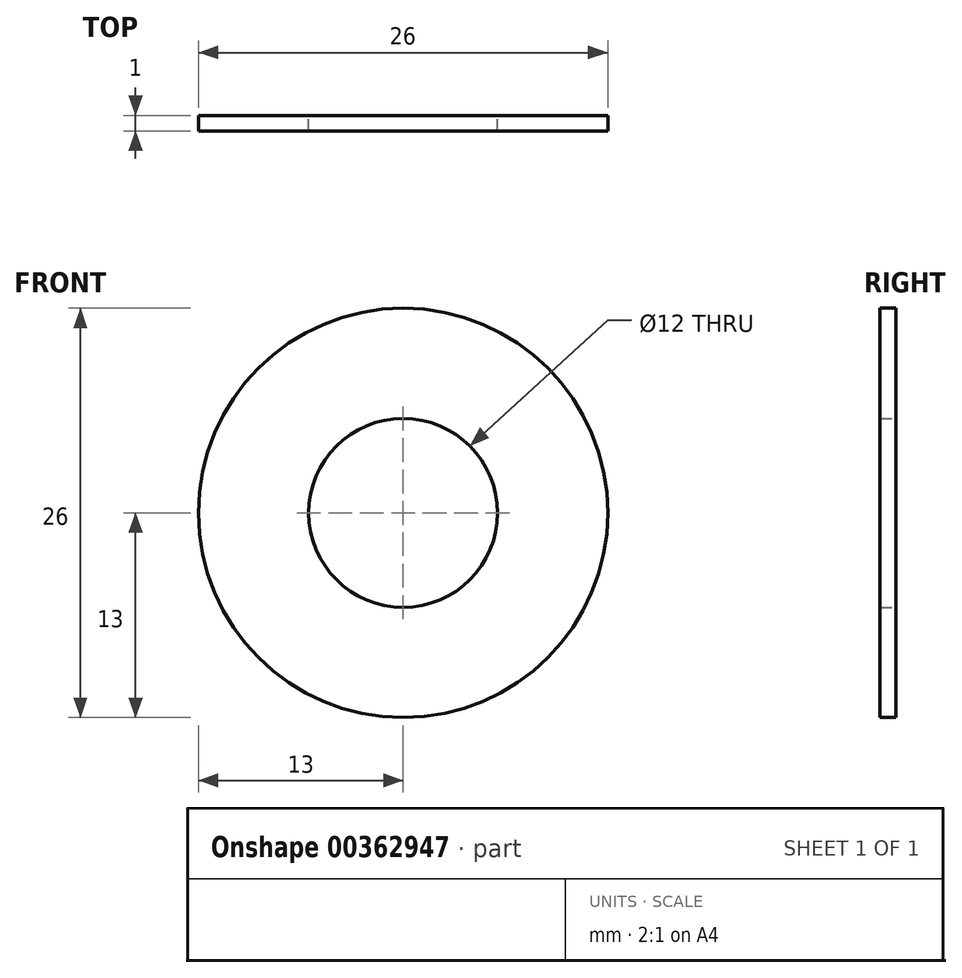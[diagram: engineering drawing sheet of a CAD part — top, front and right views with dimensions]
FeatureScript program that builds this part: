
annotation { "Feature Type Name" : "Feature", "Feature Type Description" : "" }
export const myFeature = defineFeature(function(context is Context, id is Id, definition is map)
    precondition{}
    {
        {
            var Q0;
            Q0=qCreatedBy(makeId("Front.planeOp"),FACE);
            var sketch = newSketch(context, id + "F0", { "sketchPlane" : qUnion([Q0])});
            skCircle(sketch, "E0", {"center": v(0, 0) * mm, "radius": 6 * mm});
            skCircle(sketch, "E1", {"center": v(0, 0) * mm, "radius": 13 * mm});
            skSolve(sketch);
        }
        {
            var Q0;
            Q0=makeQuery(id+"F0.imprint","IMPRINT",FACE,{"disambiguationData":[TD([[makeQuery(id+"F0.imprint","IMPRINT",EDGE,{"derivedFrom":sQuery(id+"F0.wireOp",EDGE,"E0")}),-1.0]])]});
            extrude(context, id + "F1", {"entities" : qUnion([Q0]), "depth" : 1 * mm});
        }
    });
